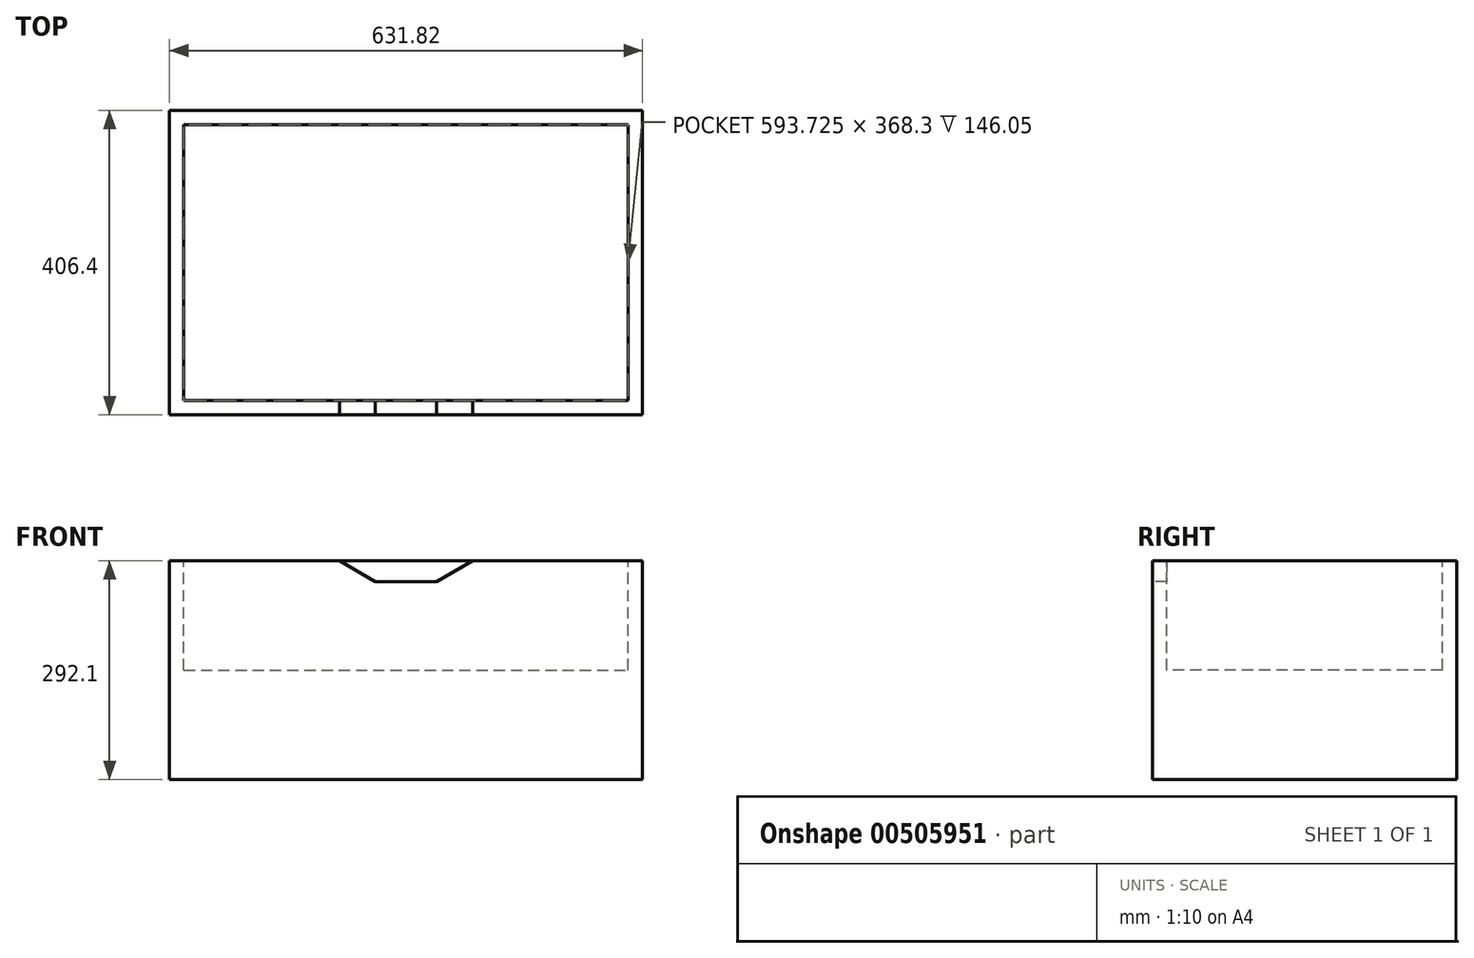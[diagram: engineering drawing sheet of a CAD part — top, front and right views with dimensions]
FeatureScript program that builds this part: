
annotation { "Feature Type Name" : "Feature", "Feature Type Description" : "" }
export const myFeature = defineFeature(function(context is Context, id is Id, definition is map)
    precondition{}
    {
        {
            var Q0;
            Q0=qCreatedBy(makeId("Top.planeOp"),FACE);
            var sketch = newSketch(context, id + "F0", { "sketchPlane" : qUnion([Q0])});
            skLineSegment(sketch, "E0.bottom", {"start": v(0, 0) * mm, "end": v(-631.83, 0) * mm});
            skLineSegment(sketch, "E0.top", {"start": v(0, 406.4) * mm, "end": v(-631.83, 406.4) * mm});
            skLineSegment(sketch, "E0.left", {"start": v(0, 0) * mm, "end": v(0, 406.4) * mm});
            skLineSegment(sketch, "E0.right", {"start": v(-631.83, 0) * mm, "end": v(-631.83, 406.4) * mm});
            skSolve(sketch);
        }
        {
            var Q0;
            Q0=qSketchRegion(id+"F0",true);
            extrude(context, id + "F1", {"entities" : qUnion([Q0]), "depth" : 292.1 * mm, "offsetDistance" : 25.4 * mm});
        }
        {
            var Q0;
            Q0=makeQuery(id+"F1.opExtrude","CAP_FACE",FACE,{"disambiguationData":[OSD([sQuery(id+"F0.wireOp",EDGE,"E0.bottom"),sQuery(id+"F0.wireOp",EDGE,"E0.top"),sQuery(id+"F0.wireOp",EDGE,"E0.left"),sQuery(id+"F0.wireOp",EDGE,"E0.right")])],"isStart":false});
            var sketch = newSketch(context, id + "F2", { "sketchPlane" : qUnion([Q0])});
            skLineSegment(sketch, "E1.bottom", {"start": v(-612.78, 387.35) * mm, "end": v(-19.05, 387.35) * mm});
            skLineSegment(sketch, "E1.top", {"start": v(-612.78, 19.05) * mm, "end": v(-19.05, 19.05) * mm});
            skLineSegment(sketch, "E1.left", {"start": v(-612.78, 387.35) * mm, "end": v(-612.78, 19.05) * mm});
            skLineSegment(sketch, "E1.right", {"start": v(-19.05, 387.35) * mm, "end": v(-19.05, 19.05) * mm});
            skSolve(sketch);
        }
        {
            var Q0;
            Q0=qSketchRegion(id+"F2",true);
            extrude(context, id + "F3", {"entities" : qUnion([Q0]), "operationType" : NewBodyOperationType.REMOVE, "oppositeDirection" : true, "depth" : 146.05 * mm, "offsetDistance" : 25.4 * mm});
        }
        {
            var Q0;
            Q0=makeQuery(id+"F1.opExtrude","SWEPT_FACE",FACE,{"disambiguationData":[OSD([sQuery(id+"F0.wireOp",EDGE,"E0.bottom")])]});
            var sketch = newSketch(context, id + "F4", { "sketchPlane" : qUnion([Q0])});
            skPoint(sketch, "E2", {"position": v(-404.81, 292.1) * mm});
            skPoint(sketch, "E3", {"position": v(-227.01, 292.1) * mm});
            skPoint(sketch, "E4", {"position": v(-356.86, 264.41) * mm});
            skPoint(sketch, "E5", {"position": v(-274.97, 264.41) * mm});
            skLineSegment(sketch, "E6", {"start": v(-404.81, 292.1) * mm, "end": v(-356.86, 264.41) * mm});
            skLineSegment(sketch, "E7", {"start": v(-227.01, 292.1) * mm, "end": v(-274.97, 264.41) * mm});
            skLineSegment(sketch, "E8", {"start": v(-356.86, 264.41) * mm, "end": v(-274.97, 264.41) * mm});
            skSolve(sketch);
        }
        {
            var Q0;
            {var subQ0=sQuery(id+"F4.wireOp",EDGE,"E6");Q0=makeQuery(id+"F4.imprint","IMPRINT",FACE,{"disambiguationData":[TD([[makeQuery(id+"F4.imprint","IMPRINT",EDGE,{"derivedFrom":subQ0}),1.0]])]});}
            extrude(context, id + "F5", {"entities" : qUnion([Q0]), "operationType" : NewBodyOperationType.REMOVE, "oppositeDirection" : true, "depth" : 66.04 * mm, "offsetDistance" : 25.4 * mm});
        }
    });
